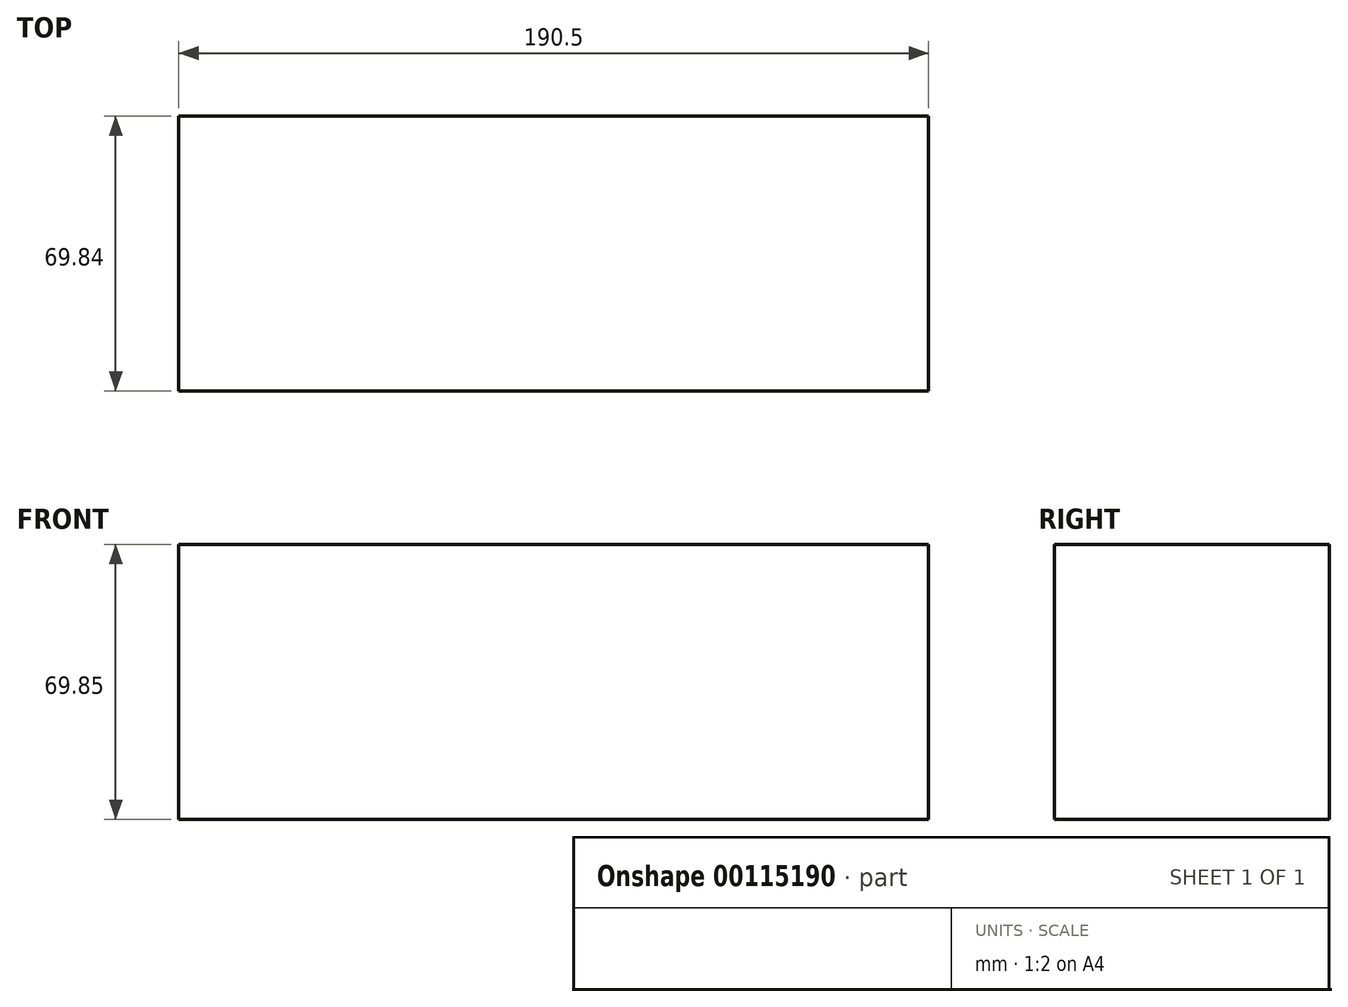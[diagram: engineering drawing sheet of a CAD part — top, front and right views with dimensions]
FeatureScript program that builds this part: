
annotation { "Feature Type Name" : "Feature", "Feature Type Description" : "" }
export const myFeature = defineFeature(function(context is Context, id is Id, definition is map)
    precondition{}
    {
        {
            var Q0;
            Q0=qCreatedBy(makeId("Top.planeOp"),FACE);
            var sketch = newSketch(context, id + "F0", { "sketchPlane" : qUnion([Q0])});
            skLineSegment(sketch, "E0.top", {"start": v(0, -34.92) * mm, "end": v(-95.25, -34.93) * mm});
            skLineSegment(sketch, "E0.right", {"start": v(-95.25, 0) * mm, "end": v(-95.25, -34.93) * mm});
            skPoint(sketch, "E1", {"position": v(-95.25, -34.93) * mm});
            skLineSegment(sketch, "E2.bottom", {"start": v(-95.25, -34.93) * mm, "end": v(95.25, -34.93) * mm});
            skLineSegment(sketch, "E2.top", {"start": v(-95.25, 34.93) * mm, "end": v(95.25, 34.93) * mm});
            skLineSegment(sketch, "E2.left", {"start": v(-95.25, -34.93) * mm, "end": v(-95.25, 34.93) * mm});
            skLineSegment(sketch, "E2.right", {"start": v(95.25, -34.92) * mm, "end": v(95.25, 34.93) * mm});
            skPoint(sketch, "E3", {"position": v(0, -34.92) * mm});
            skSolve(sketch);
        }
        {
            var Q0;
            {var subQ4=sQuery(id+"F0.wireOp",EDGE,"E2.top");Q0=makeQuery(id+"F0.imprint","IMPRINT",FACE,{"disambiguationData":[TD([[makeQuery(id+"F0.imprint","IMPRINT",EDGE,{"derivedFrom":subQ4}),-1.0]])]});}
            extrude(context, id + "F1", {"entities" : qUnion([Q0]), "depth" : 69.85 * mm});
        }
    });
